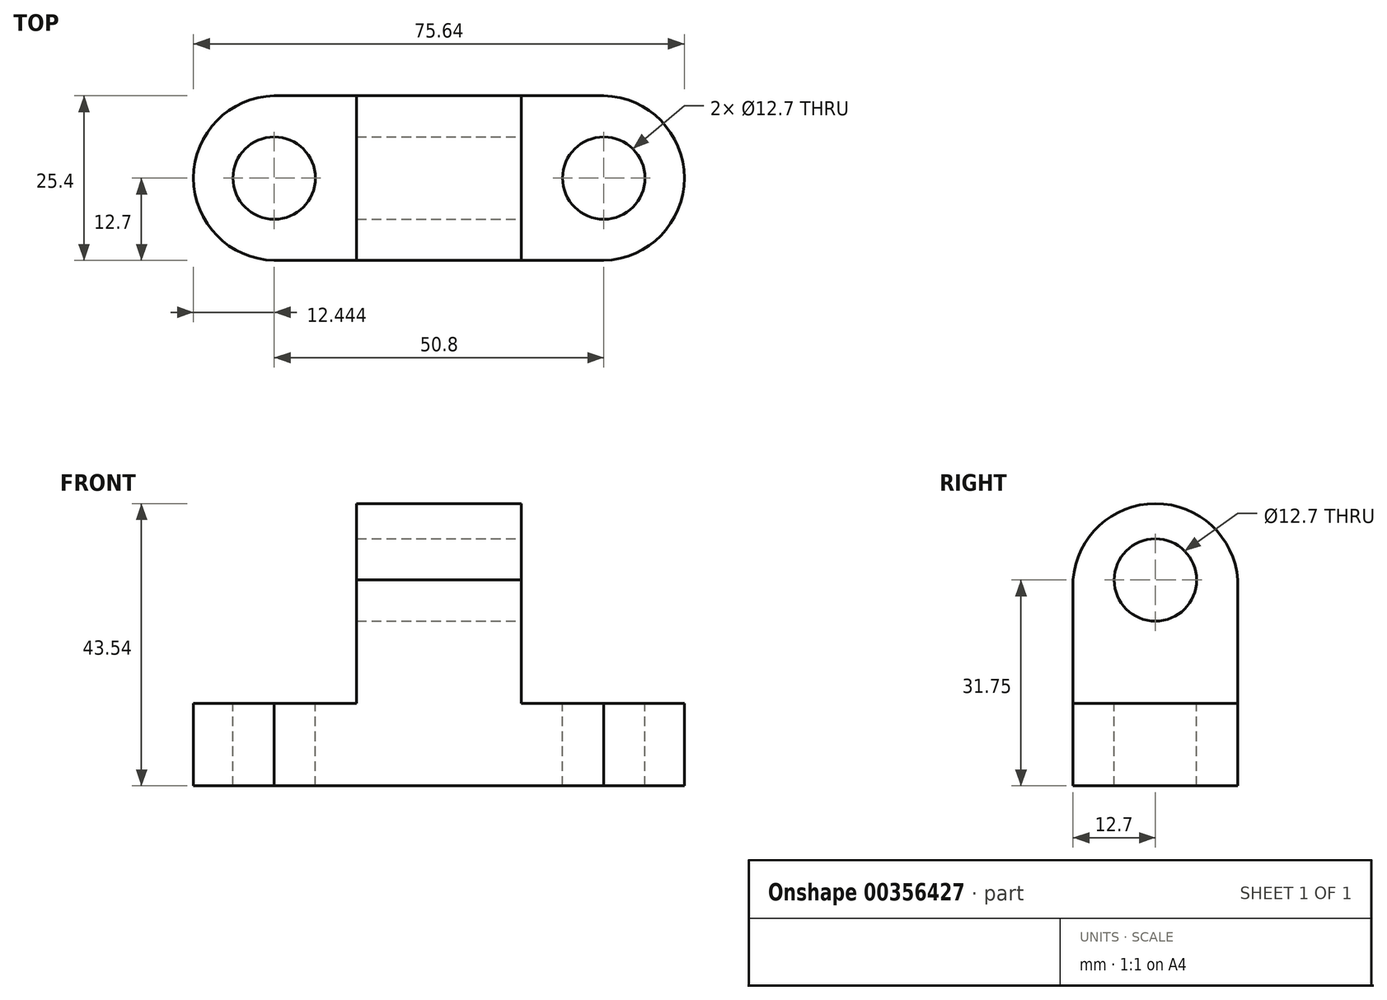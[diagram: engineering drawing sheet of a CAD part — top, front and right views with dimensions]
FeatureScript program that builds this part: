
annotation { "Feature Type Name" : "Feature", "Feature Type Description" : "" }
export const myFeature = defineFeature(function(context is Context, id is Id, definition is map)
    precondition{}
    {
        {
            var Q0;
            Q0=qCreatedBy(makeId("Top.planeOp"),FACE);
            var sketch = newSketch(context, id + "F0", { "sketchPlane" : qUnion([Q0])});
            skLineSegment(sketch, "E0", {"start": v(-35.93, 0) * mm, "end": v(40.27, 0) * mm});
            skLineSegment(sketch, "E1", {"start": v(40.27, 0) * mm, "end": v(40.27, 25.4) * mm});
            skLineSegment(sketch, "E2", {"start": v(40.27, 25.4) * mm, "end": v(-35.93, 25.4) * mm});
            skLineSegment(sketch, "E3", {"start": v(-35.93, 25.4) * mm, "end": v(-35.93, 0) * mm});
            skSolve(sketch);
        }
        {
            var Q0;
            Q0 = qSketchRegion(id + "F0", true);
            extrude(context, id + "F1", {"entities" : qUnion([Q0]), "depth" : 12.7 * mm});
        }
        {
            var Q0;
            Q0=makeQuery(id+"F1.opExtrude","CAP_FACE",FACE,{"disambiguationData":[OSD([sQuery(id+"F0.wireOp",EDGE,"E0"),sQuery(id+"F0.wireOp",EDGE,"E1"),sQuery(id+"F0.wireOp",EDGE,"E2"),sQuery(id+"F0.wireOp",EDGE,"E3")])],"isStart":false});
            var sketch = newSketch(context, id + "F2", { "sketchPlane" : qUnion([Q0])});
            skCircle(sketch, "E4", {"center": v(-23.23, 12.7) * mm, "radius": 6.35 * mm});
            skCircle(sketch, "E5", {"center": v(27.57, 12.7) * mm, "radius": 6.35 * mm});
            skSolve(sketch);
        }
        {
            var Q0;
            Q0=makeQuery(id+"F2.imprint","IMPRINT",FACE,{"disambiguationData":[TD([[makeQuery(id+"F2.imprint","IMPRINT",EDGE,{"derivedFrom":sQuery(id+"F2.wireOp",EDGE,"E4")}),1.0]])]});
            var Q1;
            Q1=makeQuery(id+"F2.imprint","IMPRINT",FACE,{"disambiguationData":[TD([[makeQuery(id+"F2.imprint","IMPRINT",EDGE,{"derivedFrom":sQuery(id+"F2.wireOp",EDGE,"E5")}),1.0]])]});
            extrude(context, id + "F3", {"entities" : qUnion([Q0, Q1]), "operationType" : NewBodyOperationType.REMOVE, "oppositeDirection" : true, "depth" : 25.4 * mm});
        }
        {
            var Q0;
            Q0=makeQuery(id+"F1.opExtrude","CAP_FACE",FACE,{"disambiguationData":[OSD([sQuery(id+"F0.wireOp",EDGE,"E0"),sQuery(id+"F0.wireOp",EDGE,"E1"),sQuery(id+"F0.wireOp",EDGE,"E2"),sQuery(id+"F0.wireOp",EDGE,"E3")])],"isStart":false});
            var sketch = newSketch(context, id + "F4", { "sketchPlane" : qUnion([Q0])});
            skLineSegment(sketch, "E6", {"start": v(-10.53, 25.4) * mm, "end": v(-10.53, 0) * mm});
            skLineSegment(sketch, "E7", {"start": v(-10.53, 0) * mm, "end": v(14.87, 0) * mm});
            skLineSegment(sketch, "E8", {"start": v(14.87, 0) * mm, "end": v(14.87, 25.4) * mm});
            skLineSegment(sketch, "E9", {"start": v(14.87, 25.4) * mm, "end": v(-10.53, 25.4) * mm});
            skSolve(sketch);
        }
        {
            var Q0;
            Q0=makeQuery(id+"F4.imprint","IMPRINT",FACE,{"disambiguationData":[TD([[makeQuery(id+"F4.imprint","IMPRINT",EDGE,{"derivedFrom":sQuery(id+"F4.wireOp",EDGE,"E6")}),1.0]])]});
            extrude(context, id + "F5", {"entities" : qUnion([Q0]), "operationType" : NewBodyOperationType.ADD, "depth" : 31.75 * mm});
        }
        {
            var Q0;
            {var subQ0=sQuery(id+"F0.wireOp",EDGE,"E2");var subQ1=sQuery(id+"F0.wireOp",EDGE,"E1");var subQ2=sQuery(id+"F0.wireOp",EDGE,"E0");Q0=makeQuery(id+"F5.boolean.opBoolean","SPLIT",FACE,{"disambiguationData":[TD([makeQuery(id+"F1.opExtrude","SWEPT_FACE",FACE,{"disambiguationData":[OSD([subQ1])]})])],"derivedFrom":makeQuery(id+"F1.opExtrude","CAP_FACE",FACE,{"disambiguationData":[OSD([subQ2,subQ1,subQ0,sQuery(id+"F0.wireOp",EDGE,"E3")])],"isStart":false})});}
            var sketch = newSketch(context, id + "F6", { "sketchPlane" : qUnion([Q0])});
            skArc(sketch, "E10", {"start": v(27.57, 0) * mm, "mid": v(39.97, 12.7) * mm, "end": v(27.57, 25.4) * mm});
            skSolve(sketch);
        }
        {
            var Q0;
            Q0 = qSketchRegion(id + "F6", true);
            var Q1;
            {var subQ0=sQuery(id+"F6.wireOp",EDGE,"E10");Q1=makeQuery(id+"F6.imprint","IMPRINT",FACE,{"disambiguationData":[TD([[makeQuery(id+"F6.imprint","IMPRINT",EDGE,{"derivedFrom":subQ0}),-1.0]])]});}
            extrude(context, id + "F7", {"entities" : qUnion([Q0, Q1]), "operationType" : NewBodyOperationType.REMOVE, "oppositeDirection" : true, "depth" : 25.4 * mm});
        }
        {
            var Q0;
            {var subQ0=sQuery(id+"F0.wireOp",EDGE,"E3");var subQ1=sQuery(id+"F0.wireOp",EDGE,"E2");var subQ2=sQuery(id+"F0.wireOp",EDGE,"E0");Q0=makeQuery(id+"F5.boolean.opBoolean","SPLIT",FACE,{"disambiguationData":[TD([makeQuery(id+"F1.opExtrude","SWEPT_FACE",FACE,{"disambiguationData":[OSD([subQ0])]})])],"derivedFrom":makeQuery(id+"F1.opExtrude","CAP_FACE",FACE,{"disambiguationData":[OSD([subQ2,sQuery(id+"F0.wireOp",EDGE,"E1"),subQ1,subQ0])],"isStart":false})});}
            var sketch = newSketch(context, id + "F8", { "sketchPlane" : qUnion([Q0])});
            skArc(sketch, "E11", {"start": v(-23.23, 25.4) * mm, "mid": v(-35.67, 12.7) * mm, "end": v(-23.23, 0) * mm});
            skSolve(sketch);
        }
        {
            var Q0;
            Q0 = qSketchRegion(id + "F8", true);
            var Q1;
            {var subQ0=sQuery(id+"F8.wireOp",EDGE,"E11");Q1=makeQuery(id+"F8.imprint","IMPRINT",FACE,{"disambiguationData":[TD([[makeQuery(id+"F8.imprint","IMPRINT",EDGE,{"derivedFrom":subQ0}),-1.0]])]});}
            extrude(context, id + "F9", {"entities" : qUnion([Q0, Q1]), "operationType" : NewBodyOperationType.REMOVE, "oppositeDirection" : true, "depth" : 25.4 * mm});
        }
        {
            var Q0;
            Q0=makeQuery(id+"F5.opExtrude","SWEPT_FACE",FACE,{"disambiguationData":[OSD([sQuery(id+"F4.wireOp",EDGE,"E8")])]});
            var sketch = newSketch(context, id + "F10", { "sketchPlane" : qUnion([Q0])});
            skCircle(sketch, "E12", {"center": v(12.7, 31.75) * mm, "radius": 6.35 * mm});
            skSolve(sketch);
        }
        {
            var Q0;
            Q0=makeQuery(id+"F10.imprint","IMPRINT",FACE,{"disambiguationData":[TD([[makeQuery(id+"F10.imprint","IMPRINT",EDGE,{"derivedFrom":sQuery(id+"F10.wireOp",EDGE,"E12")}),1.0]])]});
            extrude(context, id + "F11", {"entities" : qUnion([Q0]), "operationType" : NewBodyOperationType.REMOVE, "oppositeDirection" : true, "depth" : 25.4 * mm});
        }
        {
            var Q0;
            Q0=makeQuery(id+"F5.opExtrude","SWEPT_FACE",FACE,{"disambiguationData":[OSD([sQuery(id+"F4.wireOp",EDGE,"E8")])]});
            var sketch = newSketch(context, id + "F12", { "sketchPlane" : qUnion([Q0])});
            skArc(sketch, "E13", {"start": v(25.4, 31.75) * mm, "mid": v(12.7, 43.54) * mm, "end": v(0, 31.75) * mm});
            skSolve(sketch);
        }
        {
            var Q0;
            Q0 = qSketchRegion(id + "F12", true);
            var Q1;
            {var subQ0=sQuery(id+"F12.wireOp",EDGE,"E13");Q1=makeQuery(id+"F12.imprint","IMPRINT",FACE,{"disambiguationData":[TD([[makeQuery(id+"F12.imprint","IMPRINT",EDGE,{"derivedFrom":subQ0}),-1.0]])]});}
            extrude(context, id + "F13", {"entities" : qUnion([Q0, Q1]), "operationType" : NewBodyOperationType.REMOVE, "oppositeDirection" : true, "depth" : 25.4 * mm});
        }
    });
